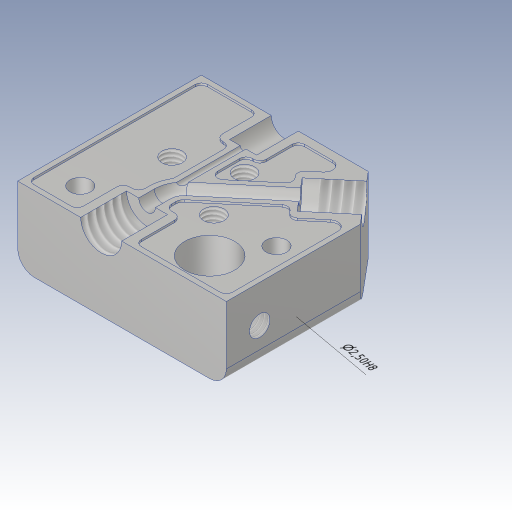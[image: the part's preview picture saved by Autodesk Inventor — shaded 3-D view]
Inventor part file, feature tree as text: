
AUTODESK INVENTOR PART (.ipt)
format: ipt  version: 2023.3 (Build 273359000, 359)  size: 509,440 bytes
history: native  units: in
note: dims shown in document units (in); Inventor stores cm internally (conversion verified against a paired STEP export)
features: sketch x9, hole x9, projected_geometry x7, extrude x3, other x2, sweep x1, revolve x1, fillet x1
ambient origin geometry x8: Origin, YZ Plane, XZ Plane, XY Plane, X Axis, Y Axis, Z Axis, Center Point
bodies: Body1 (feature_tree)
feature tree (33):
  other  "Anmerkungen"
  sketch  "Skizze3"  dims[d115=0.2362in d116=0.2362in]
  extrude  "Extrusion11"  Depth=0.2362in
  sketch  "Skizze19"  dims[d117=0.1575in d234=0.8933in]
  sweep  "Sweeping4"
  hole  "Bohrung17"  [1 undecoded]
  sketch  "Skizze20"  dims[d236=0.9843in d237=0.8661in]
  hole  "Bohrung18"  [1 undecoded]
  hole  "Bohrung27"  [1 undecoded]
  sketch  "Skizze21"  dims[d238=0.0984in d239=0.3543in d240=0.0in]
  hole  "Bohrung20"  [1 undecoded]
  revolve  "Umdrehung2"
  hole  "Bohrung28"  [1 undecoded]
  sketch  "Skizze24"  dims[d252=0.1936in d253=0.1969in d254=0.1575in d255=0.0787in d256=90.0deg d257=0.2165in d258=0.0in]
  hole  "Bohrung23"  [1 undecoded]
  fillet  "Rundung5"  Radius=0.5906in
  hole  "Bohrung24"  [1 undecoded]
  sketch  "Skizze25"  dims[d266=0.1276in d267=0.1575in d268=0.1575in d269=0.0787in d270=90.0deg d271=0.1969in d272=0.0in d273=0.0394in]
  hole  "Bohrung25"  [1 undecoded]
  hole  "Bohrung26"  [1 undecoded]
  extrude  "Extrusion12"  Depth=0.0394in
  extrude  "Extrusion14"  Depth=0.0984in
  sketch  "Skizze22"  dims[d241=0.0787in d243=0.0in d244=0.0in]
  projected_geometry  "Projizierte Kontur1"
  sketch  "Skizze23"  dims[d245=0.1936in d246=0.1575in d247=0.4961in d248=0.2598in d249=90.0deg d250=0.2165in d251=0.0in]
  projected_geometry  "Projizierte Kontur4"
  projected_geometry  "Projizierte Kontur5"
  projected_geometry  "Projizierte Kontur6"
  projected_geometry  "Projizierte Kontur10"
  projected_geometry  "Projizierte Kontur11"
  sketch  "Skizze27"  dims[d274=0.0197in d275=0.1181in d276=360.0deg d299=0.0984in d300=0.315in d301=0.1575in d302=0.0787in d303=90.0deg d304=0.2756in d305=0.0in d306=0.5906in d307=0.0787in d312=0.0968in d313=0.3937in d314=0.1575in d315=0.0787in d316=90.0deg d317=0.2992in d318=0.0in d325=0.7874in d326=0.1575in d327=0.1575in d328=0.0984in d329=0.0984in d330=0.1969in d331=0.1575in d332=0.0787in d333=90.0deg d334=0.1378in d335=0.0in d336=0.0617in d337=0.1181in d338=0.1575in d339=0.0787in d340=90.0deg d341=0.1575in d342=0.8108in d343=0.2874in d344=0.5118in d345=45.0deg d347=0.0276in d348=0.5906in d349=0.0in d350=0.0276in d351=0.2362in d352=0.1575in d353=0.0787in d354=90.0deg d355=0.4331in d356=0.0in d357=0.2559in d358=0.3937in d359=0.1575in d360=0.1378in d361=0.0in d362=360.0deg d363=0.0236in d366=0.0968in d367=0.2362in d368=0.1732in d369=0.0945in d370=0.5635in d371=0.2362in d372=0.8108in d381=0.4913in d382=0.1181in d383=0.3937in d384=0.3346in d400=0.0236in d401=0.0236in d402=0.0394in d403=0.0394in d404=0.0394in d405=0.0236in d406=0.0236in d407=0.0236in d408=0.0236in d409=0.0394in d410=0.0394in d411=0.0394in d412=0.0394in d413=0.0394in d414=0.0295in d415=0.0098in d416=0.0in d321=0.5865in d322=0.2521in d323=-0.1684in d324=0.0984in d398=0.0394in d399=0.0394in]
  projected_geometry  "Projizierte Kontur14"
  other  "Durchmesserbemaßung 1"
note: 9 required parameter values undecoded (feature->parameter linkage not recoverable at this tier; creation-order binding heuristic only, values carry confidence <= 0.55)
